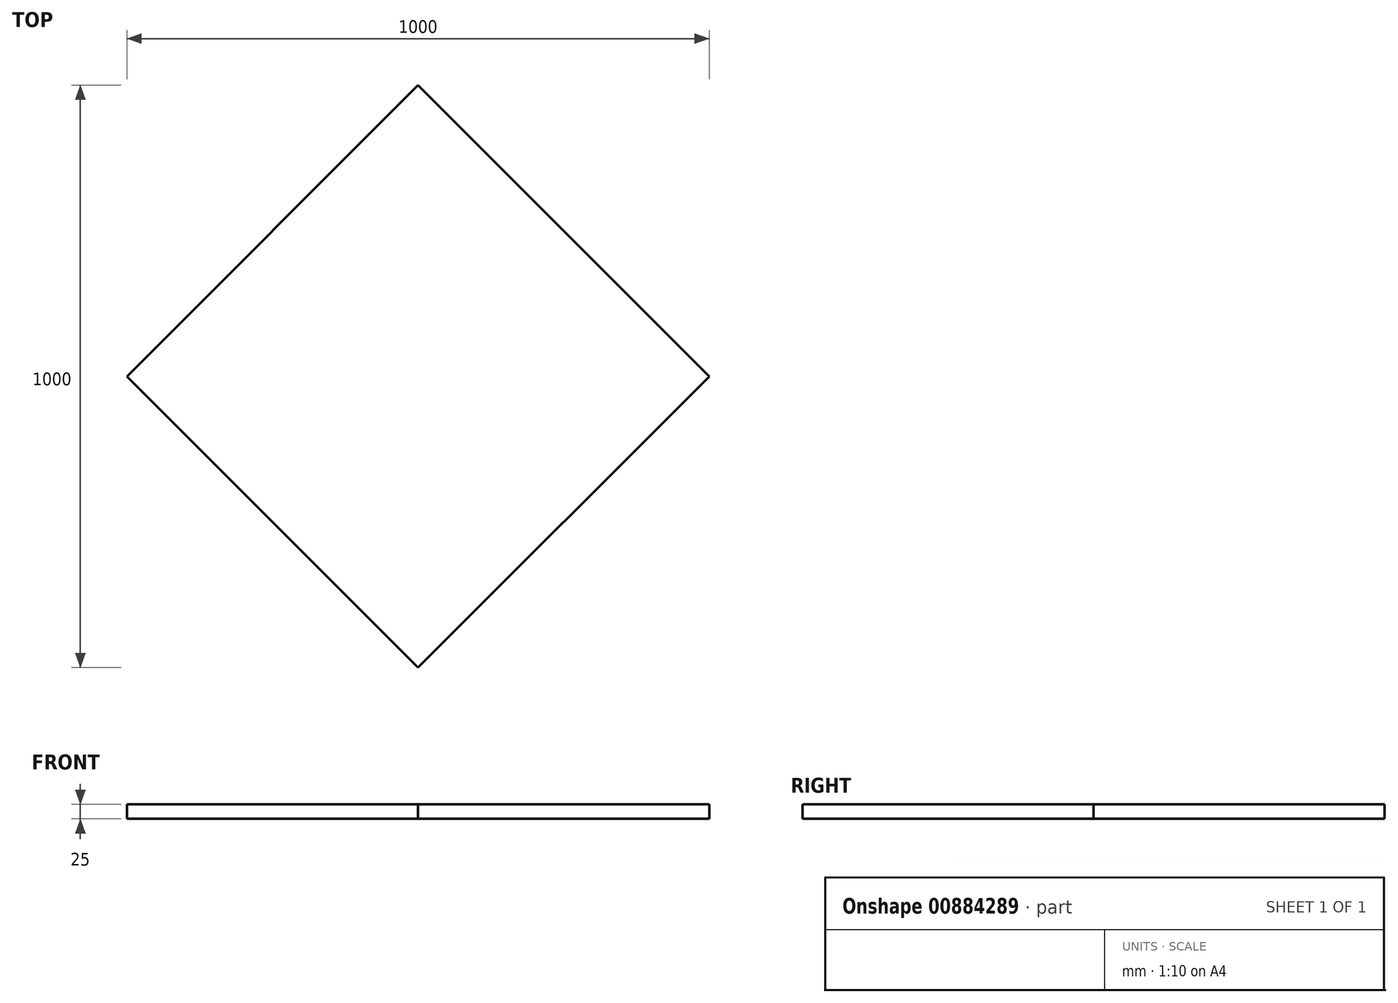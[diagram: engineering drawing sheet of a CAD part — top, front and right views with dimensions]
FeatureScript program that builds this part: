
annotation { "Feature Type Name" : "Feature", "Feature Type Description" : "" }
export const myFeature = defineFeature(function(context is Context, id is Id, definition is map)
    precondition{}
    {
        {
            var Q0;
            Q0=qCreatedBy(makeId("Top.planeOp"),FACE);
            var sketch = newSketch(context, id + "F0", { "sketchPlane" : qUnion([Q0])});
            skLineSegment(sketch, "E0.bottom", {"start": v(250, -250) * mm, "end": v(-250, -250) * mm});
            skLineSegment(sketch, "E0.top", {"start": v(250, 250) * mm, "end": v(-250, 250) * mm});
            skLineSegment(sketch, "E0.left", {"start": v(250, -250) * mm, "end": v(250, 250) * mm});
            skLineSegment(sketch, "E0.right", {"start": v(-250, -250) * mm, "end": v(-250, 250) * mm});
            skPoint(sketch, "E0.middle", {"position": v(0, 0) * mm});
            skSolve(sketch);
        }
        {
            var Q0;
            Q0=makeQuery(id+"F0.imprint","IMPRINT",FACE,{"disambiguationData":[TD([[makeQuery(id+"F0.imprint","IMPRINT",EDGE,{"derivedFrom":sQuery(id+"F0.wireOp",EDGE,"E0.bottom")}),-1.0]])]});
            cPlane(context, id + "F1", {"entities" : qUnion([Q0]), "cplaneType" : CPlaneType.OFFSET, "offset" : 500 * mm, "width" : 150 * mm, "height" : 150 * mm});
        }
        {
            var Q0;
            Q0=qCreatedBy(id+"F1.planeOp",FACE);
            var sketch = newSketch(context, id + "F2", { "sketchPlane" : qUnion([Q0])});
            skPoint(sketch, "E1.0", {"position": v(-250, 250) * mm});
            skPoint(sketch, "E2.0", {"position": v(250, 250) * mm});
            skPoint(sketch, "E3.0", {"position": v(250, -250) * mm});
            skPoint(sketch, "E4.0", {"position": v(-250, -250) * mm});
            skPoint(sketch, "E5.0", {"position": v(0, 0) * mm});
            skLineSegment(sketch, "E6", {"start": v(-250, -250) * mm, "end": v(0, 0) * mm});
            skLineSegment(sketch, "E7", {"start": v(0, 0) * mm, "end": v(250, 250) * mm});
            skLineSegment(sketch, "E8", {"start": v(0, 0) * mm, "end": v(250, -250) * mm, "construction": true});
            skLineSegment(sketch, "E9", {"start": v(0, 0) * mm, "end": v(-250, 250) * mm, "construction": true});
            skLineSegment(sketch, "E10", {"start": v(-250, -250) * mm, "end": v(0, -500) * mm});
            skLineSegment(sketch, "E11", {"start": v(0, -500) * mm, "end": v(0, -500) * mm});
            skLineSegment(sketch, "E12", {"start": v(0, -500) * mm, "end": v(250, -250) * mm});
            skLineSegment(sketch, "E13", {"start": v(250, -250) * mm, "end": v(250, -250) * mm});
            skLineSegment(sketch, "E14", {"start": v(250, 250) * mm, "end": v(500, 0) * mm});
            skLineSegment(sketch, "E15", {"start": v(500, 0) * mm, "end": v(250, 250) * mm});
            skLineSegment(sketch, "E16", {"start": v(250, 250) * mm, "end": v(-250, -250) * mm, "construction": true});
            skLineSegment(sketch, "E17", {"start": v(-500, 0) * mm, "end": v(-250, -250) * mm});
            skLineSegment(sketch, "E18", {"start": v(-500, 0) * mm, "end": v(-250, 250) * mm});
            skLineSegment(sketch, "E19", {"start": v(-250, 250) * mm, "end": v(0, 500) * mm});
            skLineSegment(sketch, "E20", {"start": v(0, 500) * mm, "end": v(250, 250) * mm});
            skLineSegment(sketch, "E21", {"start": v(500, 0) * mm, "end": v(250, -250) * mm});
            skSolve(sketch);
        }
        {
            var Q0;
            Q0=sQuery(id+"F0.wireOp",VERTEX,"E0.bottom.start");
            var Q1;
            Q1=sQuery(id+"F2.wireOp",VERTEX,"E15.start");
            var Q2;
            Q2=sQuery(id+"F2.wireOp",VERTEX,"E12.start");
            cPlane(context, id + "F3", {"entities" : qUnion([Q0, Q1, Q2]), "cplaneType" : CPlaneType.THREE_POINT, "offset" : 25 * mm, "width" : 150 * mm, "height" : 150 * mm});
        }
        {
            var Q0;
            Q0=sQuery(id+"F0.wireOp",VERTEX,"E0.left.end");
            var Q1;
            Q1=sQuery(id+"F2.wireOp",VERTEX,"E15.start");
            var Q2;
            Q2=sQuery(id+"F2.wireOp",VERTEX,"E19.end");
            cPlane(context, id + "F4", {"entities" : qUnion([Q0, Q1, Q2]), "cplaneType" : CPlaneType.THREE_POINT, "offset" : 25 * mm, "width" : 150 * mm, "height" : 150 * mm});
        }
        {
            var Q0;
            Q0=sQuery(id+"F2.wireOp",VERTEX,"E18.start");
            var Q1;
            Q1=sQuery(id+"F2.wireOp",VERTEX,"E19.end");
            var Q2;
            Q2=sQuery(id+"F0.wireOp",VERTEX,"E0.top.end");
            cPlane(context, id + "F5", {"entities" : qUnion([Q0, Q1, Q2]), "cplaneType" : CPlaneType.THREE_POINT, "offset" : 25 * mm, "width" : 150 * mm, "height" : 150 * mm});
        }
        {
            var Q0;
            Q0=sQuery(id+"F2.wireOp",VERTEX,"E18.start");
            var Q1;
            Q1=sQuery(id+"F2.wireOp",VERTEX,"E12.start");
            var Q2;
            Q2=sQuery(id+"F0.wireOp",VERTEX,"E0.bottom.end");
            cPlane(context, id + "F6", {"entities" : qUnion([Q0, Q1, Q2]), "cplaneType" : CPlaneType.THREE_POINT, "offset" : 25 * mm, "width" : 150 * mm, "height" : 150 * mm});
        }
        {
            var Q0;
            Q0=qCreatedBy(id+"F6.planeOp",FACE);
            var sketch = newSketch(context, id + "F7", { "sketchPlane" : qUnion([Q0])});
            skPoint(sketch, "E22.0", {"position": v(0, 0) * mm});
            skPoint(sketch, "E23.0", {"position": v(353.55, 500) * mm});
            skPoint(sketch, "E24.0", {"position": v(-353.55, 500) * mm});
            skLineSegment(sketch, "E25", {"start": v(353.55, 500) * mm, "end": v(0, 0) * mm});
            skLineSegment(sketch, "E26", {"start": v(0, 0) * mm, "end": v(-353.55, 500) * mm});
            skSolve(sketch);
        }
        {
            var Q0;
            Q0=qCreatedBy(id+"F3.planeOp",FACE);
            var sketch = newSketch(context, id + "F8", { "sketchPlane" : qUnion([Q0])});
            skPoint(sketch, "E27.0", {"position": v(353.55, 500) * mm});
            skPoint(sketch, "E28.0", {"position": v(-353.55, 500) * mm});
            skPoint(sketch, "E29.0", {"position": v(0, 0) * mm});
            skLineSegment(sketch, "E30", {"start": v(353.55, 500) * mm, "end": v(0, 0) * mm});
            skLineSegment(sketch, "E31", {"start": v(0, 0) * mm, "end": v(-353.55, 500) * mm});
            skSolve(sketch);
        }
        {
            var Q0;
            Q0=qCreatedBy(id+"F4.planeOp",FACE);
            var sketch = newSketch(context, id + "F9", { "sketchPlane" : qUnion([Q0])});
            skPoint(sketch, "E32.0", {"position": v(353.55, 500) * mm});
            skPoint(sketch, "E33.0", {"position": v(-353.55, 500) * mm});
            skPoint(sketch, "E34.0", {"position": v(0, 0) * mm});
            skLineSegment(sketch, "E35", {"start": v(-353.55, 500) * mm, "end": v(0, 0) * mm});
            skLineSegment(sketch, "E36", {"start": v(0, 0) * mm, "end": v(353.55, 500) * mm});
            skSolve(sketch);
        }
        {
            var Q0;
            Q0=makeQuery(id+"F2.imprint","IMPRINT",FACE,{"disambiguationData":[TD([[makeQuery(id+"F2.imprint","IMPRINT",EDGE,{"derivedFrom":sQuery(id+"F2.wireOp",EDGE,"E6")}),1.0]])]});
            var Q1;
            Q1=makeQuery(id+"F2.imprint","IMPRINT",FACE,{"disambiguationData":[TD([[makeQuery(id+"F2.imprint","IMPRINT",EDGE,{"derivedFrom":sQuery(id+"F2.wireOp",EDGE,"E6")}),-1.0]])]});
            extrude(context, id + "F10", {"entities" : qUnion([Q0, Q1]), "depth" : 25 * mm, "offsetDistance" : 25 * mm});
        }
    });
